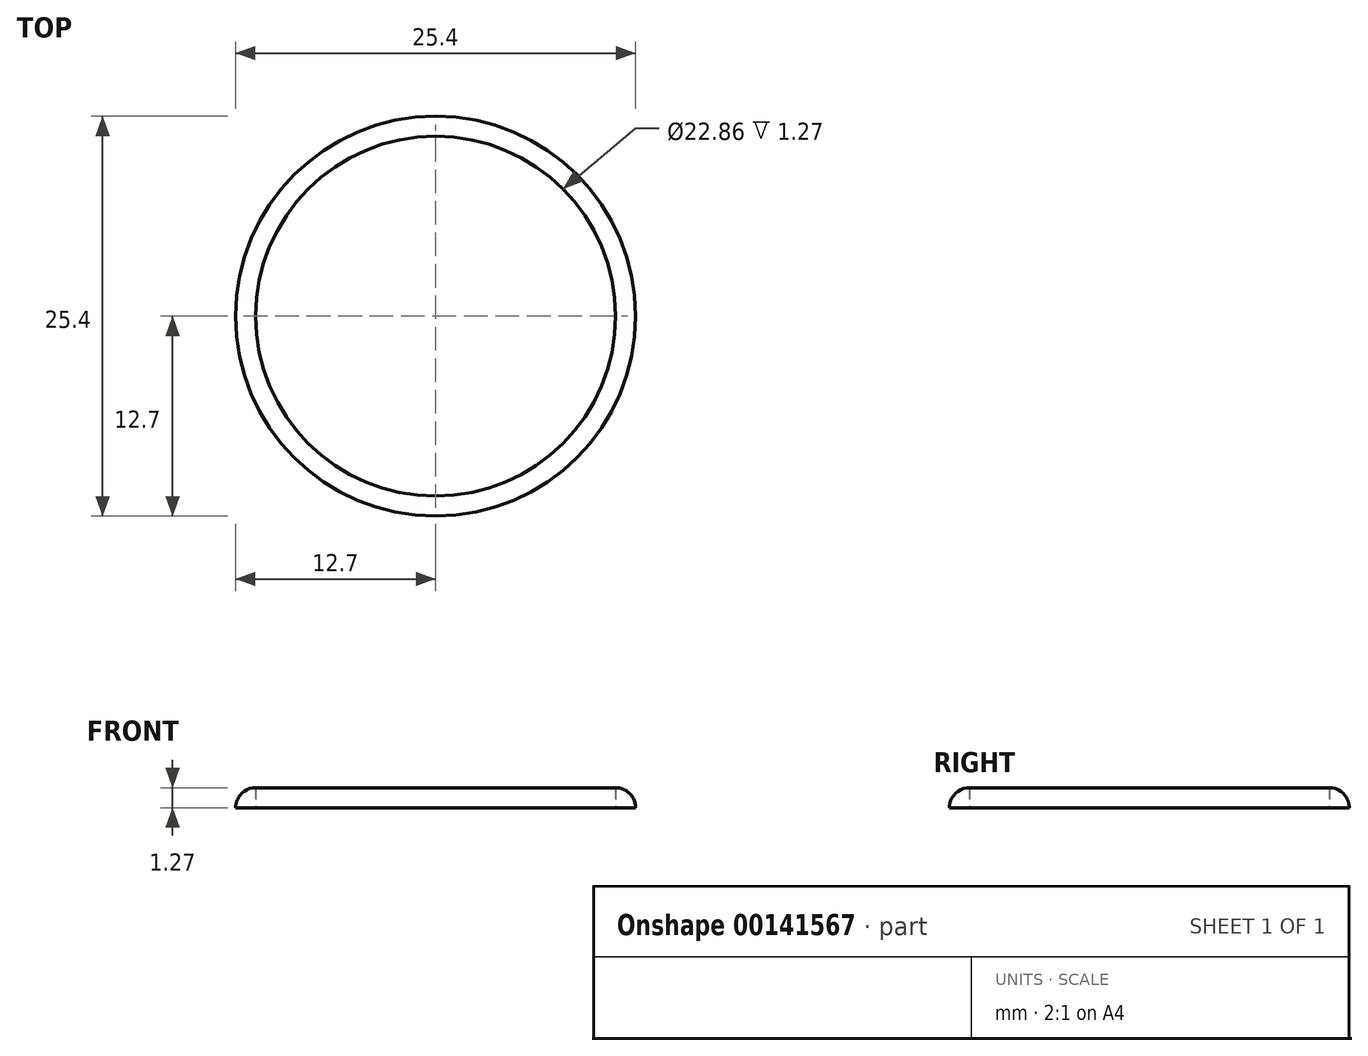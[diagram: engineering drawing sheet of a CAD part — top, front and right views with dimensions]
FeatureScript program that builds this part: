
annotation { "Feature Type Name" : "Feature", "Feature Type Description" : "" }
export const myFeature = defineFeature(function(context is Context, id is Id, definition is map)
    precondition{}
    {
        {
            var Q0;
            Q0=qCreatedBy(makeId("Top.planeOp"),FACE);
            var sketch = newSketch(context, id + "F0", { "sketchPlane" : qUnion([Q0])});
            skCircle(sketch, "E0", {"center": v(0, 0) * mm, "radius": 11.43 * mm});
            skCircle(sketch, "E1", {"center": v(0, 0) * mm, "radius": 12.7 * mm});
            skSolve(sketch);
        }
        {
            var Q0;
            Q0=makeQuery(id+"F0.imprint","IMPRINT",FACE,{"disambiguationData":[TD([[makeQuery(id+"F0.imprint","IMPRINT",EDGE,{"derivedFrom":sQuery(id+"F0.wireOp",EDGE,"E0")}),-1.0]])]});
            extrude(context, id + "F1", {"entities" : qUnion([Q0]), "depth" : 1.27 * mm});
        }
        {
            var Q0;
            Q0=makeQuery(id+"F1.opExtrude","CAP_EDGE",EDGE,{"disambiguationData":[OSD([sQuery(id+"F0.wireOp",EDGE,"E1")])],"isStart":false});
            fillet(context, id + "F2", {"entities" : qUnion([Q0]), "radius" : 1.27 * mm, "tangentPropagation" : true, "allowEdgeOverflow" : false});
        }
    });
